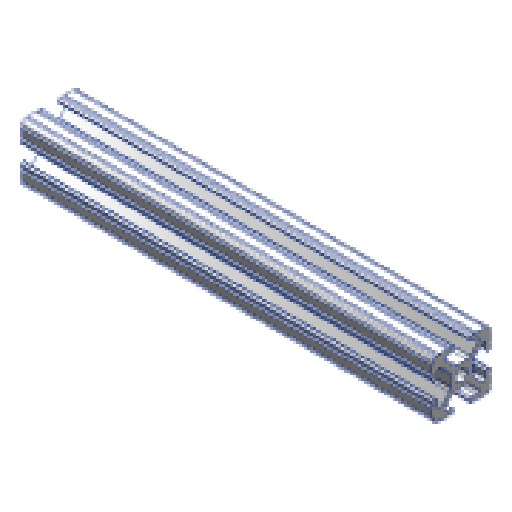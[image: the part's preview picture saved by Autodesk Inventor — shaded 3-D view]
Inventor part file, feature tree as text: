
AUTODESK INVENTOR PART (.ipt)
format: ipt  version: 2025 (Build 290162000, 162)  size: 219,136 bytes
history: native  units: in
note: dims shown in document units (in); Inventor stores cm internally (conversion verified against a paired STEP export)
features: extrude x1, sketch x1
ambient origin geometry x8: Origin, YZ Plane, XZ Plane, XY Plane, X Axis, Y Axis, Z Axis, Center Point
bodies: Solid1 (feature_tree)
feature tree (2):
  extrude  "Extrusion1"  [1 undecoded]
  sketch  "Sketch1"  dims[d0=7.0in d1=0.0in]
note: 1 required parameter value undecoded (feature->parameter linkage not recoverable at this tier; creation-order binding heuristic only, values carry confidence <= 0.55)
